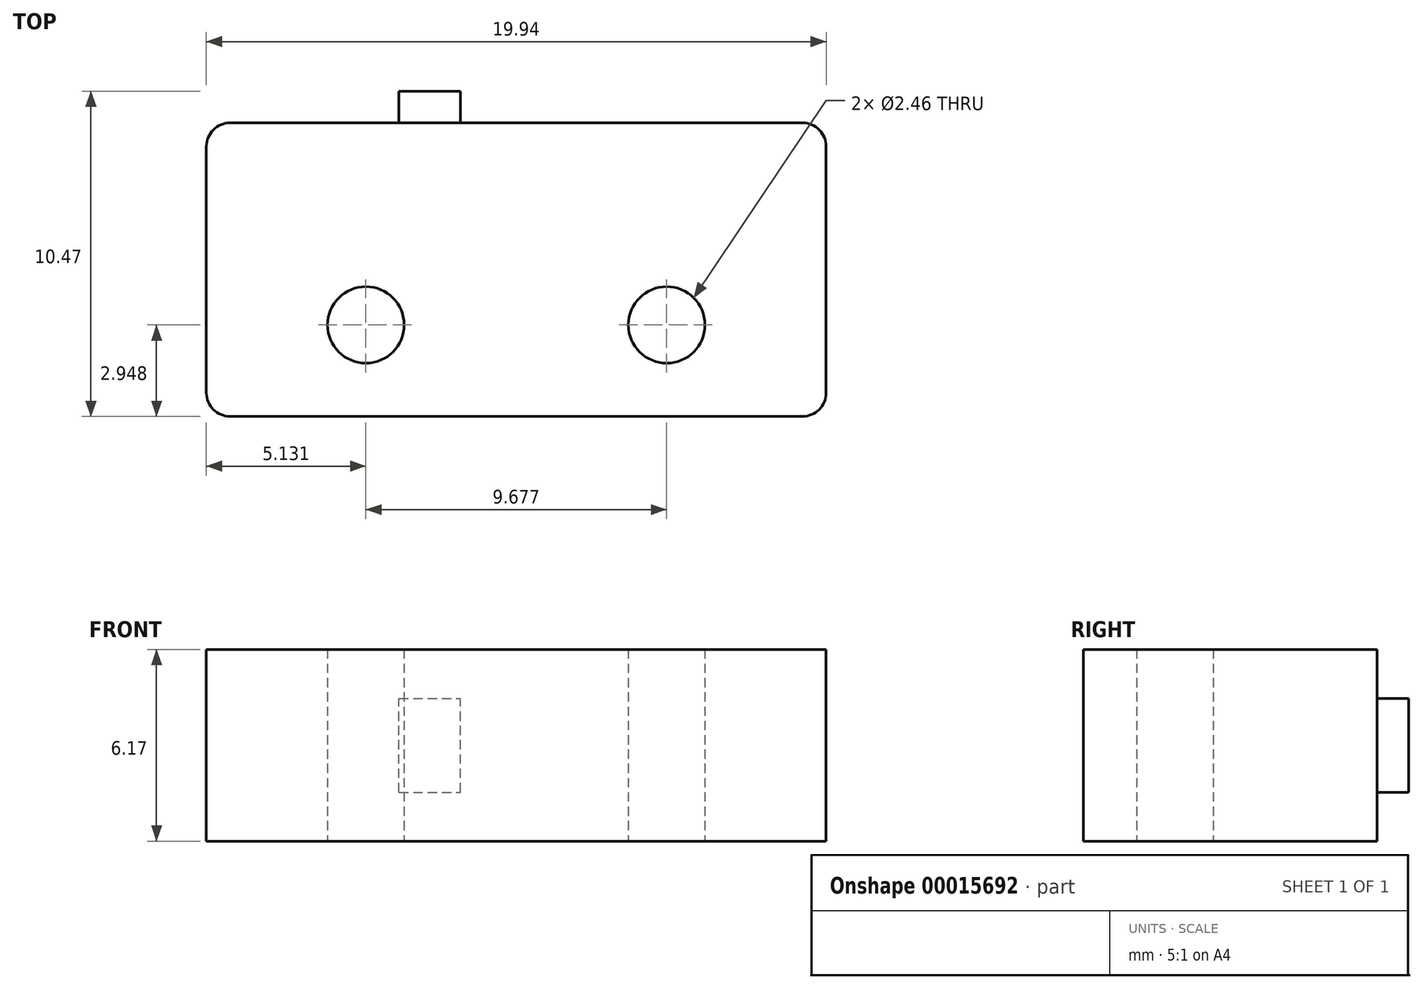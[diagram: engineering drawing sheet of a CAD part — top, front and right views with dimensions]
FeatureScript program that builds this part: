
annotation { "Feature Type Name" : "Feature", "Feature Type Description" : "" }
export const myFeature = defineFeature(function(context is Context, id is Id, definition is map)
    precondition{}
    {
        {
            var Q0;
            Q0=qCreatedBy(makeId("Top.planeOp"),FACE);
            var sketch = newSketch(context, id + "F0", { "sketchPlane" : qUnion([Q0])});
            skLineSegment(sketch, "E0.bottom", {"start": v(0, 0) * mm, "end": v(19.94, 0) * mm});
            skLineSegment(sketch, "E0.top", {"start": v(0, -9.45) * mm, "end": v(19.94, -9.45) * mm});
            skLineSegment(sketch, "E0.left", {"start": v(0, 0) * mm, "end": v(0, -9.45) * mm});
            skLineSegment(sketch, "E0.right", {"start": v(19.94, 0) * mm, "end": v(19.94, -9.45) * mm});
            skLineSegment(sketch, "E1", {"start": v(9.97, -9.45) * mm, "end": v(9.97, -6.5) * mm, "construction": true});
            skLineSegment(sketch, "E2", {"start": v(5.13, -6.5) * mm, "end": v(14.8, -6.5) * mm, "construction": true});
            skCircle(sketch, "E3", {"center": v(5.13, -6.5) * mm, "radius": 1.23 * mm});
            skCircle(sketch, "E4", {"center": v(14.8, -6.5) * mm, "radius": 1.23 * mm});
            skSolve(sketch);
        }
        {
            var Q0;
            Q0 = qSketchRegion(id + "F0", true);
            extrude(context, id + "F1", {"entities" : qUnion([Q0]), "depth" : 6.17 * mm});
        }
        {
            var Q0;
            Q0=makeQuery(id+"F1.opExtrude","SWEPT_FACE",FACE,{"disambiguationData":[OSD([sQuery(id+"F0.wireOp",EDGE,"E0.bottom")])]});
            var sketch = newSketch(context, id + "F2", { "sketchPlane" : qUnion([Q0])});
            skLineSegment(sketch, "E5", {"start": v(0, 3.09) * mm, "end": v(-6.2, 3.09) * mm});
            skLineSegment(sketch, "E6.bottom", {"start": v(-6.2, 1.57) * mm, "end": v(-8.18, 1.57) * mm});
            skLineSegment(sketch, "E6.top", {"start": v(-6.2, 4.6) * mm, "end": v(-8.18, 4.6) * mm});
            skLineSegment(sketch, "E6.left", {"start": v(-6.2, 1.57) * mm, "end": v(-6.2, 4.6) * mm});
            skLineSegment(sketch, "E6.right", {"start": v(-8.18, 1.57) * mm, "end": v(-8.18, 4.6) * mm});
            skSolve(sketch);
        }
        {
            var Q0;
            Q0 = qSketchRegion(id + "F2", true);
            extrude(context, id + "F3", {"entities" : qUnion([Q0]), "operationType" : NewBodyOperationType.ADD, "depth" : 1.02 * mm});
        }
        {
            var Q0;
            Q0=makeQuery(id+"F1.opExtrude","SWEPT_EDGE",EDGE,{"disambiguationData":[OSD([sQuery(id+"F0.wireOp",EDGE,"E0.bottom"),sQuery(id+"F0.wireOp",EDGE,"E0.right")])]});
            var Q1;
            Q1=makeQuery(id+"F1.opExtrude","SWEPT_EDGE",EDGE,{"disambiguationData":[OSD([sQuery(id+"F0.wireOp",EDGE,"E0.bottom"),sQuery(id+"F0.wireOp",EDGE,"E0.left")])]});
            var Q2;
            Q2=makeQuery(id+"F1.opExtrude","SWEPT_EDGE",EDGE,{"disambiguationData":[OSD([sQuery(id+"F0.wireOp",EDGE,"E0.top"),sQuery(id+"F0.wireOp",EDGE,"E0.left")])]});
            var Q3;
            Q3=makeQuery(id+"F1.opExtrude","SWEPT_EDGE",EDGE,{"disambiguationData":[OSD([sQuery(id+"F0.wireOp",EDGE,"E0.top"),sQuery(id+"F0.wireOp",EDGE,"E0.right")])]});
            fillet(context, id + "F4", {"entities" : qUnion([Q0, Q1, Q2, Q3]), "radius" : 0.76 * mm, "tangentPropagation" : true, "allowEdgeOverflow" : false});
        }
    });
